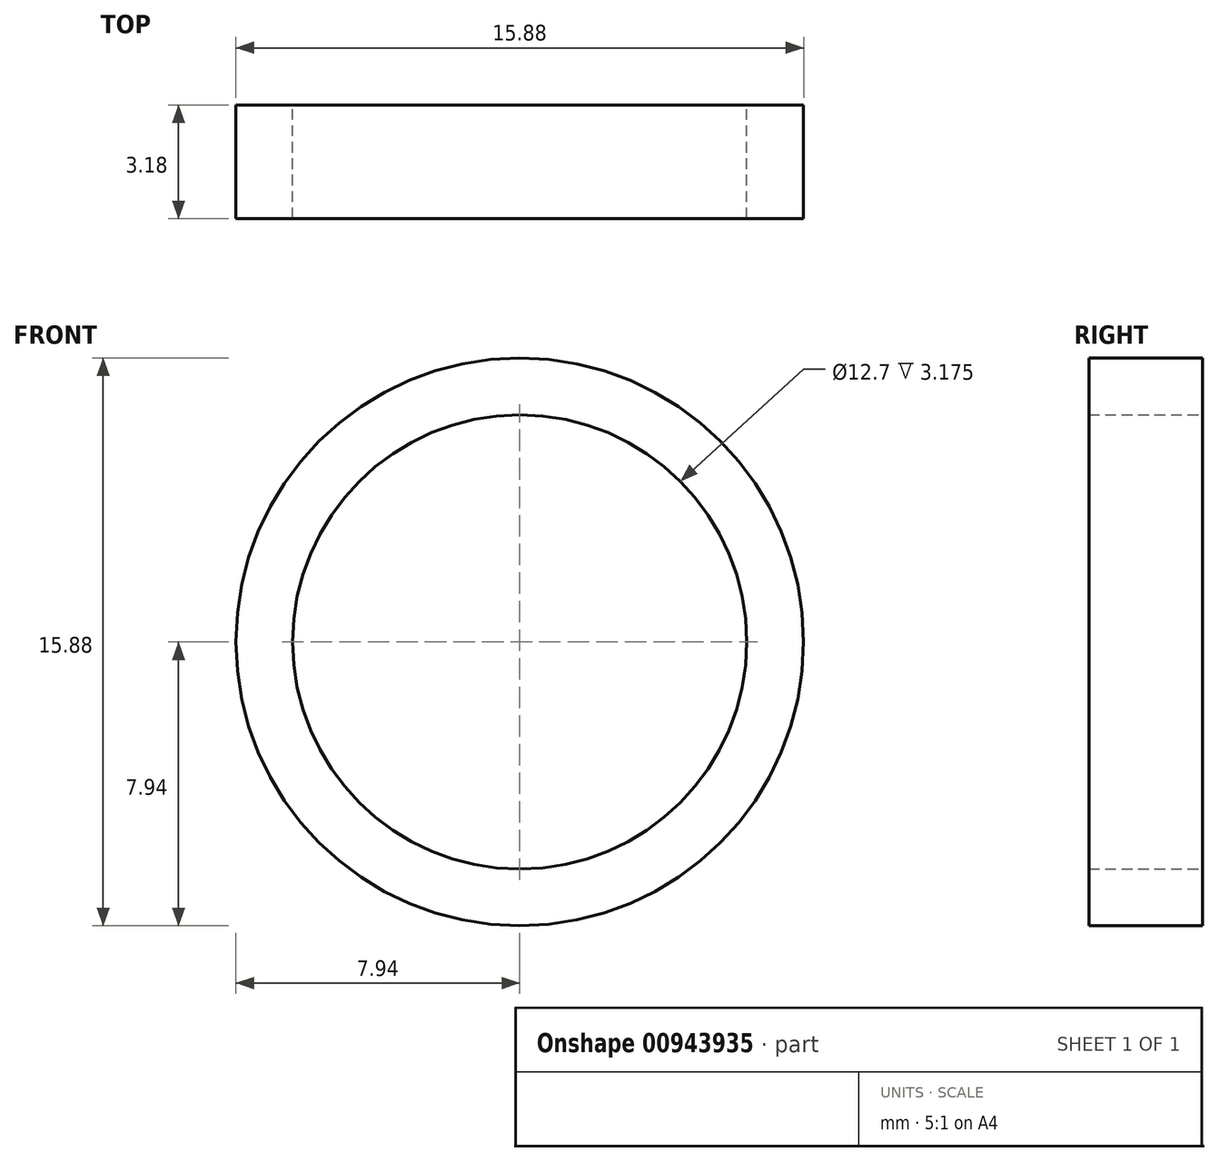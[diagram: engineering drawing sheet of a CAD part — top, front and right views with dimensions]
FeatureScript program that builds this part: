
annotation { "Feature Type Name" : "Feature", "Feature Type Description" : "" }
export const myFeature = defineFeature(function(context is Context, id is Id, definition is map)
    precondition{}
    {
        {
            var Q0;
            Q0=qCreatedBy(makeId("Front.planeOp"),FACE);
            var sketch = newSketch(context, id + "F0", { "sketchPlane" : qUnion([Q0])});
            skLineSegment(sketch, "E0", {"start": v(0, 0) * mm, "end": v(-6.35, 0) * mm});
            skLineSegment(sketch, "E1", {"start": v(-6.35, 0) * mm, "end": v(-7.94, 0) * mm});
            skCircle(sketch, "E2", {"center": v(0, 0) * mm, "radius": 6.35 * mm});
            skCircle(sketch, "E3", {"center": v(0, 0) * mm, "radius": 7.94 * mm});
            skSolve(sketch);
        }
        {
            var Q0;
            Q0 = qSketchRegion(id + "F0", true);
            extrude(context, id + "F1", {"entities" : qUnion([Q0]), "depth" : 3.17 * mm, "offsetDistance" : 25.4 * mm});
        }
    });
